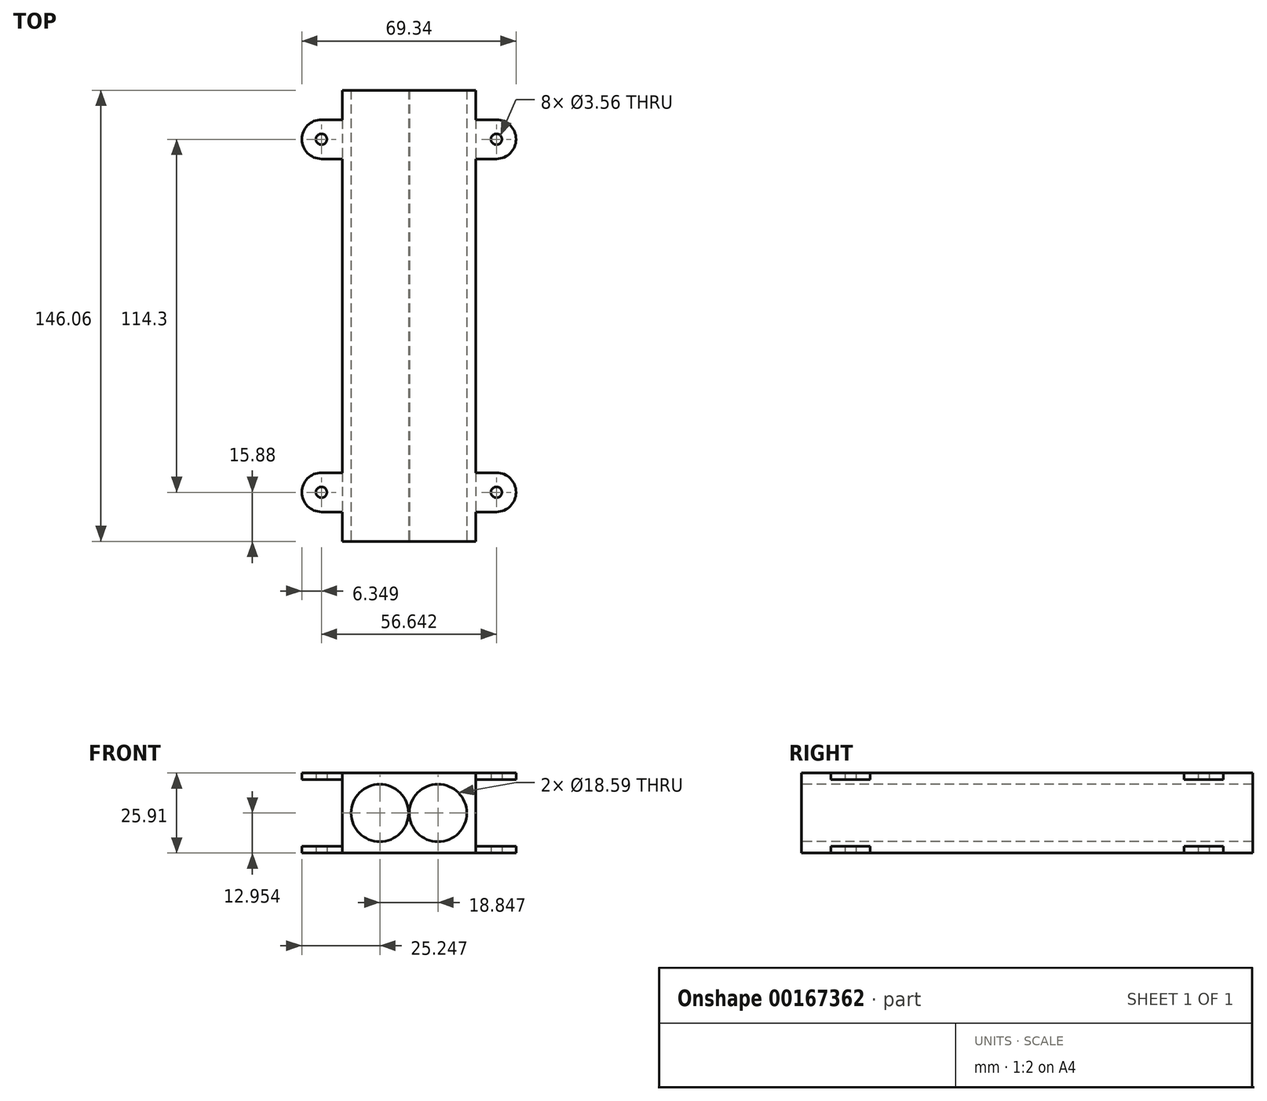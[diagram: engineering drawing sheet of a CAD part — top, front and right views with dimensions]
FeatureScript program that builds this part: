
annotation { "Feature Type Name" : "Feature", "Feature Type Description" : "" }
export const myFeature = defineFeature(function(context is Context, id is Id, definition is map)
    precondition{}
    {
        {
            var Q0;
            Q0=qCreatedBy(makeId("Top.planeOp"),FACE);
            var sketch = newSketch(context, id + "F0", { "sketchPlane" : qUnion([Q0])});
            skLineSegment(sketch, "E0.bottom", {"start": v(21.59, 73.02) * mm, "end": v(-21.59, 73.02) * mm});
            skLineSegment(sketch, "E0.top", {"start": v(21.59, -73.02) * mm, "end": v(-21.59, -73.02) * mm});
            skLineSegment(sketch, "E0.left", {"start": v(21.59, 73.02) * mm, "end": v(21.59, -73.02) * mm});
            skLineSegment(sketch, "E0.right", {"start": v(-21.59, 73.02) * mm, "end": v(-21.59, -73.02) * mm});
            skPoint(sketch, "E0.middle", {"position": v(0, 0) * mm});
            skLineSegment(sketch, "E1.bottom", {"start": v(21.59, 63.5) * mm, "end": v(28.32, 63.5) * mm});
            skLineSegment(sketch, "E1.top", {"start": v(21.59, 50.8) * mm, "end": v(28.32, 50.8) * mm});
            skLineSegment(sketch, "E1.left", {"start": v(21.59, 63.5) * mm, "end": v(21.59, 50.8) * mm});
            skLineSegment(sketch, "E1.right", {"start": v(28.32, 63.5) * mm, "end": v(28.32, 50.8) * mm, "construction": true});
            skArc(sketch, "E2", {"start": v(28.32, 50.8) * mm, "mid": v(34.67, 57.15) * mm, "end": v(28.32, 63.5) * mm});
            skCircle(sketch, "E3", {"center": v(28.32, 57.15) * mm, "radius": 1.78 * mm});
            skLineSegment(sketch, "E4.bottom", {"start": v(21.59, -50.8) * mm, "end": v(28.32, -50.8) * mm});
            skLineSegment(sketch, "E4.top", {"start": v(21.59, -63.5) * mm, "end": v(28.32, -63.5) * mm});
            skLineSegment(sketch, "E4.left", {"start": v(21.59, -50.8) * mm, "end": v(21.59, -63.5) * mm});
            skLineSegment(sketch, "E4.right", {"start": v(28.32, -50.8) * mm, "end": v(28.32, -63.5) * mm, "construction": true});
            skArc(sketch, "E5", {"start": v(28.32, -63.5) * mm, "mid": v(34.67, -57.15) * mm, "end": v(28.32, -50.8) * mm});
            skCircle(sketch, "E6", {"center": v(28.32, -57.15) * mm, "radius": 1.78 * mm});
            skLineSegment(sketch, "E7.bottom", {"start": v(-21.59, 50.8) * mm, "end": v(-28.32, 50.8) * mm});
            skLineSegment(sketch, "E7.top", {"start": v(-21.59, 63.5) * mm, "end": v(-28.32, 63.5) * mm});
            skLineSegment(sketch, "E7.left", {"start": v(-21.59, 50.8) * mm, "end": v(-21.59, 63.5) * mm});
            skLineSegment(sketch, "E7.right", {"start": v(-28.32, 50.8) * mm, "end": v(-28.32, 63.5) * mm, "construction": true});
            skArc(sketch, "E8", {"start": v(-28.32, 63.5) * mm, "mid": v(-34.67, 57.15) * mm, "end": v(-28.32, 50.8) * mm});
            skCircle(sketch, "E9", {"center": v(-28.32, 57.15) * mm, "radius": 1.78 * mm});
            skLineSegment(sketch, "E10.bottom", {"start": v(-21.59, -63.5) * mm, "end": v(-28.32, -63.5) * mm});
            skLineSegment(sketch, "E10.top", {"start": v(-21.59, -50.8) * mm, "end": v(-28.32, -50.8) * mm});
            skLineSegment(sketch, "E10.left", {"start": v(-21.59, -63.5) * mm, "end": v(-21.59, -50.8) * mm});
            skLineSegment(sketch, "E10.right", {"start": v(-28.32, -63.5) * mm, "end": v(-28.32, -50.8) * mm, "construction": true});
            skArc(sketch, "E11", {"start": v(-28.32, -50.8) * mm, "mid": v(-34.67, -57.15) * mm, "end": v(-28.32, -63.5) * mm});
            skCircle(sketch, "E12", {"center": v(-28.32, -57.15) * mm, "radius": 1.78 * mm});
            skLineSegment(sketch, "E13", {"start": v(-21.59, 63.5) * mm, "end": v(21.59, 63.5) * mm, "construction": true});
            skLineSegment(sketch, "E14", {"start": v(-21.59, -50.8) * mm, "end": v(21.59, -50.8) * mm, "construction": true});
            skSolve(sketch);
        }
        {
            var Q0;
            Q0 = qSketchRegion(id + "F0", true);
            extrude(context, id + "F1", {"entities" : qUnion([Q0]), "depth" : 2.16 * mm});
        }
        {
            var Q0;
            Q0=makeQuery(id+"F1.opExtrude","CAP_FACE",FACE,{"disambiguationData":[OSD([sQuery(id+"F0.wireOp",EDGE,"E0.bottom"),sQuery(id+"F0.wireOp",EDGE,"E0.top"),sQuery(id+"F0.wireOp",EDGE,"E0.left"),sQuery(id+"F0.wireOp",EDGE,"E0.right"),sQuery(id+"F0.wireOp",EDGE,"E1.bottom"),sQuery(id+"F0.wireOp",EDGE,"E1.top"),sQuery(id+"F0.wireOp",EDGE,"E2"),sQuery(id+"F0.wireOp",EDGE,"E3"),sQuery(id+"F0.wireOp",EDGE,"E4.bottom"),sQuery(id+"F0.wireOp",EDGE,"E4.top"),sQuery(id+"F0.wireOp",EDGE,"E5"),sQuery(id+"F0.wireOp",EDGE,"E6"),sQuery(id+"F0.wireOp",EDGE,"E7.bottom"),sQuery(id+"F0.wireOp",EDGE,"E7.top"),sQuery(id+"F0.wireOp",EDGE,"E8"),sQuery(id+"F0.wireOp",EDGE,"E9"),sQuery(id+"F0.wireOp",EDGE,"E10.bottom"),sQuery(id+"F0.wireOp",EDGE,"E10.top"),sQuery(id+"F0.wireOp",EDGE,"E11"),sQuery(id+"F0.wireOp",EDGE,"E12")])],"isStart":false});
            var sketch = newSketch(context, id + "F2", { "sketchPlane" : qUnion([Q0])});
            skLineSegment(sketch, "E15.bottom", {"start": v(-21.59, 73.02) * mm, "end": v(21.59, 73.02) * mm});
            skLineSegment(sketch, "E15.top", {"start": v(-21.59, -73.02) * mm, "end": v(21.59, -73.02) * mm});
            skLineSegment(sketch, "E15.left", {"start": v(-21.59, 73.02) * mm, "end": v(-21.59, -73.02) * mm});
            skLineSegment(sketch, "E15.right", {"start": v(21.59, 73.02) * mm, "end": v(21.59, -73.02) * mm});
            skSolve(sketch);
        }
        {
            var Q0;
            Q0 = qSketchRegion(id + "F2", true);
            extrude(context, id + "F3", {"entities" : qUnion([Q0]), "operationType" : NewBodyOperationType.ADD, "depth" : 21.59 * mm});
        }
        {
            var Q0;
            Q0=makeQuery(id+"F3.opExtrude","CAP_FACE",FACE,{"disambiguationData":[OSD([sQuery(id+"F2.wireOp",EDGE,"E15.bottom"),sQuery(id+"F2.wireOp",EDGE,"E15.top"),sQuery(id+"F2.wireOp",EDGE,"E15.left"),sQuery(id+"F2.wireOp",EDGE,"E15.right")])],"isStart":false});
            var sketch = newSketch(context, id + "F4", { "sketchPlane" : qUnion([Q0])});
            skLineSegment(sketch, "E16.bottom", {"start": v(21.59, 73.02) * mm, "end": v(-21.59, 73.02) * mm});
            skLineSegment(sketch, "E16.top", {"start": v(21.59, -73.03) * mm, "end": v(-21.59, -73.03) * mm});
            skLineSegment(sketch, "E16.left", {"start": v(21.59, 73.02) * mm, "end": v(21.6, -73.03) * mm});
            skLineSegment(sketch, "E16.right", {"start": v(-21.59, 73.02) * mm, "end": v(-21.59, -73.03) * mm});
            skPoint(sketch, "E16.middle", {"position": v(0, 0) * mm});
            skLineSegment(sketch, "E17.bottom", {"start": v(21.6, 63.5) * mm, "end": v(28.32, 63.5) * mm});
            skLineSegment(sketch, "E17.top", {"start": v(21.59, 50.8) * mm, "end": v(28.32, 50.8) * mm});
            skLineSegment(sketch, "E17.left", {"start": v(21.59, 63.5) * mm, "end": v(21.59, 50.8) * mm});
            skLineSegment(sketch, "E17.right", {"start": v(28.32, 63.5) * mm, "end": v(28.32, 50.8) * mm, "construction": true});
            skArc(sketch, "E18", {"start": v(28.32, 50.8) * mm, "mid": v(34.67, 57.15) * mm, "end": v(28.32, 63.5) * mm});
            skCircle(sketch, "E19", {"center": v(28.32, 57.15) * mm, "radius": 1.78 * mm});
            skLineSegment(sketch, "E20.bottom", {"start": v(21.6, -50.8) * mm, "end": v(28.32, -50.8) * mm});
            skLineSegment(sketch, "E20.top", {"start": v(21.59, -63.5) * mm, "end": v(28.32, -63.5) * mm});
            skLineSegment(sketch, "E20.left", {"start": v(21.6, -50.8) * mm, "end": v(21.6, -63.5) * mm});
            skLineSegment(sketch, "E20.right", {"start": v(28.32, -50.8) * mm, "end": v(28.32, -63.5) * mm, "construction": true});
            skArc(sketch, "E21", {"start": v(28.32, -63.5) * mm, "mid": v(34.67, -57.15) * mm, "end": v(28.32, -50.8) * mm});
            skCircle(sketch, "E22", {"center": v(28.32, -57.15) * mm, "radius": 1.78 * mm});
            skLineSegment(sketch, "E23.bottom", {"start": v(-21.59, 50.8) * mm, "end": v(-28.32, 50.8) * mm});
            skLineSegment(sketch, "E23.top", {"start": v(-21.59, 63.5) * mm, "end": v(-28.32, 63.5) * mm});
            skLineSegment(sketch, "E23.left", {"start": v(-21.59, 50.8) * mm, "end": v(-21.59, 63.5) * mm});
            skLineSegment(sketch, "E23.right", {"start": v(-28.32, 50.8) * mm, "end": v(-28.32, 63.5) * mm, "construction": true});
            skArc(sketch, "E24", {"start": v(-28.32, 63.5) * mm, "mid": v(-34.67, 57.15) * mm, "end": v(-28.32, 50.8) * mm});
            skCircle(sketch, "E25", {"center": v(-28.32, 57.15) * mm, "radius": 1.78 * mm});
            skLineSegment(sketch, "E26.bottom", {"start": v(-21.59, -63.5) * mm, "end": v(-28.32, -63.5) * mm});
            skLineSegment(sketch, "E26.top", {"start": v(-21.59, -50.8) * mm, "end": v(-28.32, -50.8) * mm});
            skLineSegment(sketch, "E26.left", {"start": v(-21.59, -63.5) * mm, "end": v(-21.59, -50.8) * mm});
            skLineSegment(sketch, "E26.right", {"start": v(-28.32, -63.5) * mm, "end": v(-28.32, -50.8) * mm, "construction": true});
            skArc(sketch, "E27", {"start": v(-28.32, -50.8) * mm, "mid": v(-34.67, -57.15) * mm, "end": v(-28.32, -63.5) * mm});
            skCircle(sketch, "E28", {"center": v(-28.32, -57.15) * mm, "radius": 1.78 * mm});
            skLineSegment(sketch, "E29", {"start": v(-21.59, 63.5) * mm, "end": v(21.6, 63.5) * mm, "construction": true});
            skLineSegment(sketch, "E30", {"start": v(-21.59, -50.8) * mm, "end": v(21.6, -50.8) * mm, "construction": true});
            skSolve(sketch);
        }
        {
            var Q0;
            Q0 = qSketchRegion(id + "F4", true);
            extrude(context, id + "F5", {"entities" : qUnion([Q0]), "operationType" : NewBodyOperationType.ADD, "depth" : 2.16 * mm});
        }
        {
            var Q0;
            Q0=makeQuery(id+"F5.boolean.opBoolean","MERGE",FACE,{"derivedFrom":[makeQuery(id+"F3.boolean.opBoolean","MERGE",FACE,{"derivedFrom":[makeQuery(id+"F1.opExtrude","SWEPT_FACE",FACE,{"disambiguationData":[OSD([sQuery(id+"F0.wireOp",EDGE,"E0.top")])]}),makeQuery(id+"F3.opExtrude","SWEPT_FACE",FACE,{"disambiguationData":[OSD([sQuery(id+"F2.wireOp",EDGE,"E15.top")])]})]}),makeQuery(id+"F5.opExtrude","SWEPT_FACE",FACE,{"disambiguationData":[OSD([sQuery(id+"F4.wireOp",EDGE,"E16.top")])]})]});
            var sketch = newSketch(context, id + "F6", { "sketchPlane" : qUnion([Q0])});
            skCircle(sketch, "E31", {"center": v(-9.42, 12.95) * mm, "radius": 9.3 * mm});
            skLineSegment(sketch, "E32", {"start": v(-21.59, 12.95) * mm, "end": v(21.6, 12.95) * mm, "construction": true});
            skCircle(sketch, "E33", {"center": v(9.42, 12.95) * mm, "radius": 9.3 * mm});
            skLineSegment(sketch, "E34", {"start": v(-21.59, 12.95) * mm, "end": v(-18.72, 12.95) * mm, "construction": true});
            skLineSegment(sketch, "E35", {"start": v(21.6, 12.95) * mm, "end": v(18.72, 12.95) * mm, "construction": true});
            skLineSegment(sketch, "E36.bottom", {"start": v(-0.63, 15.99) * mm, "end": v(0.64, 15.99) * mm});
            skLineSegment(sketch, "E36.top", {"start": v(-0.63, 9.92) * mm, "end": v(0.64, 9.92) * mm});
            skLineSegment(sketch, "E36.left", {"start": v(-0.63, 15.99) * mm, "end": v(-0.63, 9.92) * mm});
            skLineSegment(sketch, "E36.right", {"start": v(0.64, 15.99) * mm, "end": v(0.64, 9.92) * mm});
            skSolve(sketch);
        }
        {
            var Q0;
            {var subQ0=sQuery(id+"F6.wireOp",EDGE,"E36.left");Q0=makeQuery(id+"F6.imprint","IMPRINT",FACE,{"disambiguationData":[TD([[makeQuery(id+"F6.imprint","IMPRINT",EDGE,{"derivedFrom":subQ0}),-1.0]])]});}
            var Q1;
            {var subQ0=sQuery(id+"F6.wireOp",EDGE,"E36.left");Q1=makeQuery(id+"F6.imprint","IMPRINT",FACE,{"disambiguationData":[TD([[makeQuery(id+"F6.imprint","IMPRINT",EDGE,{"derivedFrom":subQ0}),1.0]])]});}
            var Q2;
            {var subQ0=sQuery(id+"F6.wireOp",EDGE,"E36.right");Q2=makeQuery(id+"F6.imprint","IMPRINT",FACE,{"disambiguationData":[TD([[makeQuery(id+"F6.imprint","IMPRINT",EDGE,{"derivedFrom":subQ0}),-1.0]])]});}
            var Q3;
            {var subQ0=sQuery(id+"F6.wireOp",EDGE,"E36.right");Q3=makeQuery(id+"F6.imprint","IMPRINT",FACE,{"disambiguationData":[TD([[makeQuery(id+"F6.imprint","IMPRINT",EDGE,{"derivedFrom":subQ0}),1.0]])]});}
            extrude(context, id + "F7", {"entities" : qUnion([Q0, Q1, Q2, Q3]), "operationType" : NewBodyOperationType.REMOVE, "endBound" : BoundingType.THROUGH_ALL, "oppositeDirection" : true, "depth" : 25.4 * mm});
        }
    });
